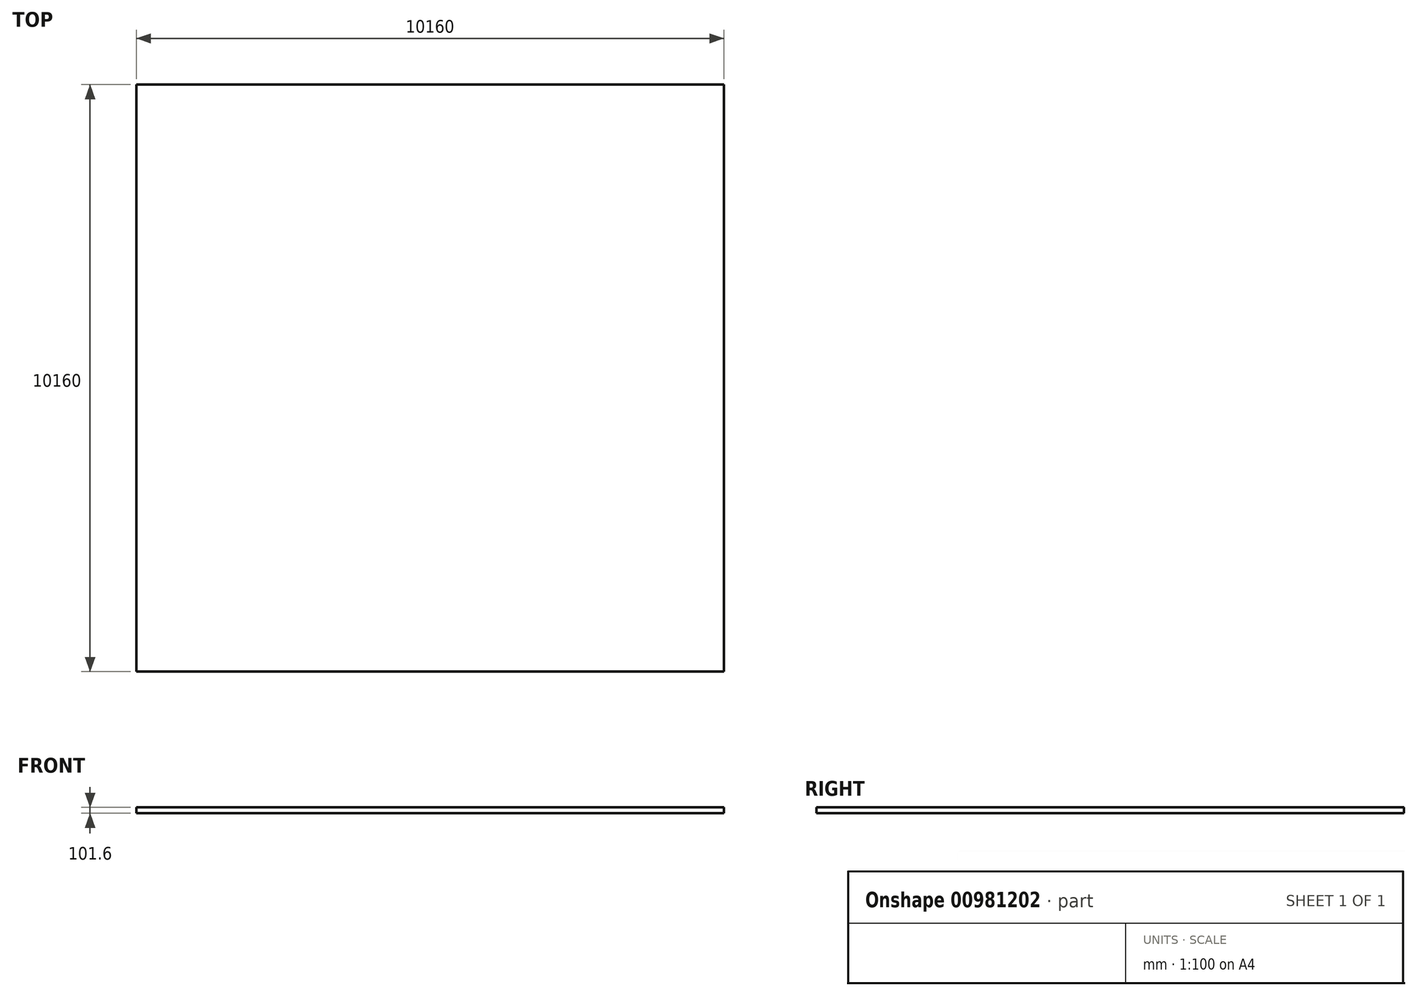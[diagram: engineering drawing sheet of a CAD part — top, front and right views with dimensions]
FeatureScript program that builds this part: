
annotation { "Feature Type Name" : "Feature", "Feature Type Description" : "" }
export const myFeature = defineFeature(function(context is Context, id is Id, definition is map)
    precondition{}
    {
        {
            var Q0;
            Q0=qCreatedBy(makeId("Top.planeOp"),FACE);
            var sketch = newSketch(context, id + "F0", { "sketchPlane" : qUnion([Q0])});
            skLineSegment(sketch, "E0.bottom", {"start": v(-5080, 5080) * mm, "end": v(5080, 5080) * mm});
            skLineSegment(sketch, "E0.top", {"start": v(-5080, -5080) * mm, "end": v(5080, -5080) * mm});
            skLineSegment(sketch, "E0.left", {"start": v(-5080, 5080) * mm, "end": v(-5080, -5080) * mm});
            skLineSegment(sketch, "E0.right", {"start": v(5080, 5080) * mm, "end": v(5080, -5080) * mm});
            skPoint(sketch, "E0.middle", {"position": v(0, 0) * mm});
            skSolve(sketch);
        }
        {
            var Q0;
            Q0 = qSketchRegion(id + "F0", true);
            extrude(context, id + "F1", {"entities" : qUnion([Q0]), "oppositeDirection" : true, "depth" : 101.6 * mm, "offsetDistance" : 25.4 * mm});
        }
    });
